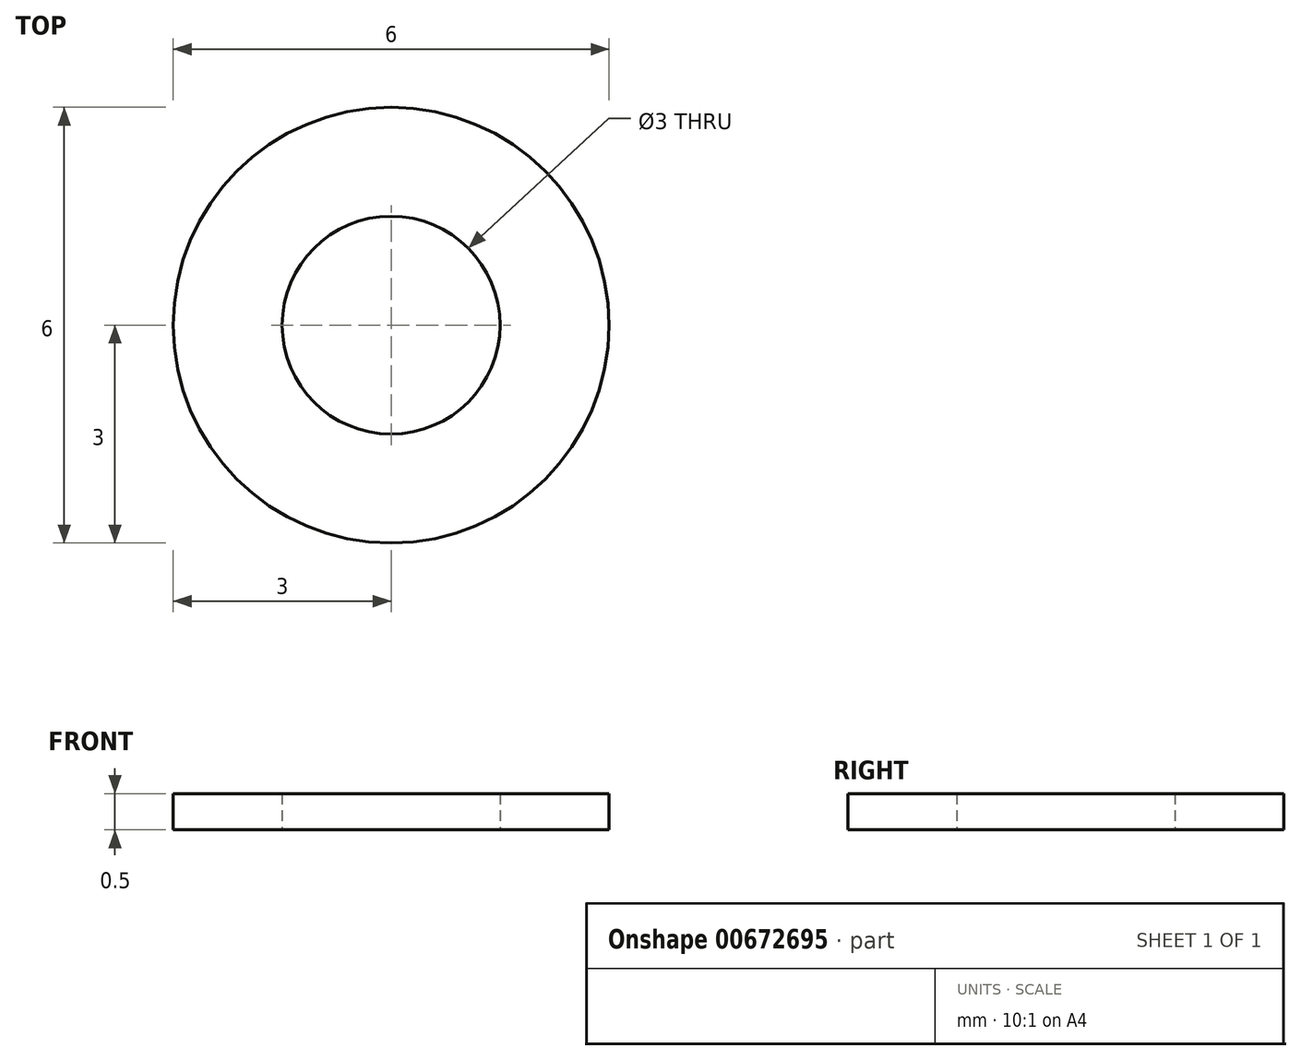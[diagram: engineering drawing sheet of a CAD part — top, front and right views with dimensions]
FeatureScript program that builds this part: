
annotation { "Feature Type Name" : "Feature", "Feature Type Description" : "" }
export const myFeature = defineFeature(function(context is Context, id is Id, definition is map)
    precondition{}
    {
        {
            var Q0;
            Q0=qCreatedBy(makeId("Top.planeOp"),FACE);
            var sketch = newSketch(context, id + "F0", { "sketchPlane" : qUnion([Q0])});
            skCircle(sketch, "E0", {"center": v(0, 0) * mm, "radius": 3 * mm});
            skCircle(sketch, "E1", {"center": v(0, 0) * mm, "radius": 1.5 * mm});
            skSolve(sketch);
        }
        {
            var Q0;
            Q0=makeQuery(id+"F0.imprint","IMPRINT",FACE,{"disambiguationData":[TD([[makeQuery(id+"F0.imprint","IMPRINT",EDGE,{"derivedFrom":sQuery(id+"F0.wireOp",EDGE,"E0")}),1.0]])]});
            extrude(context, id + "F1", {"entities" : qUnion([Q0]), "depth" : 0.5 * mm, "offsetDistance" : 25 * mm});
        }
    });
